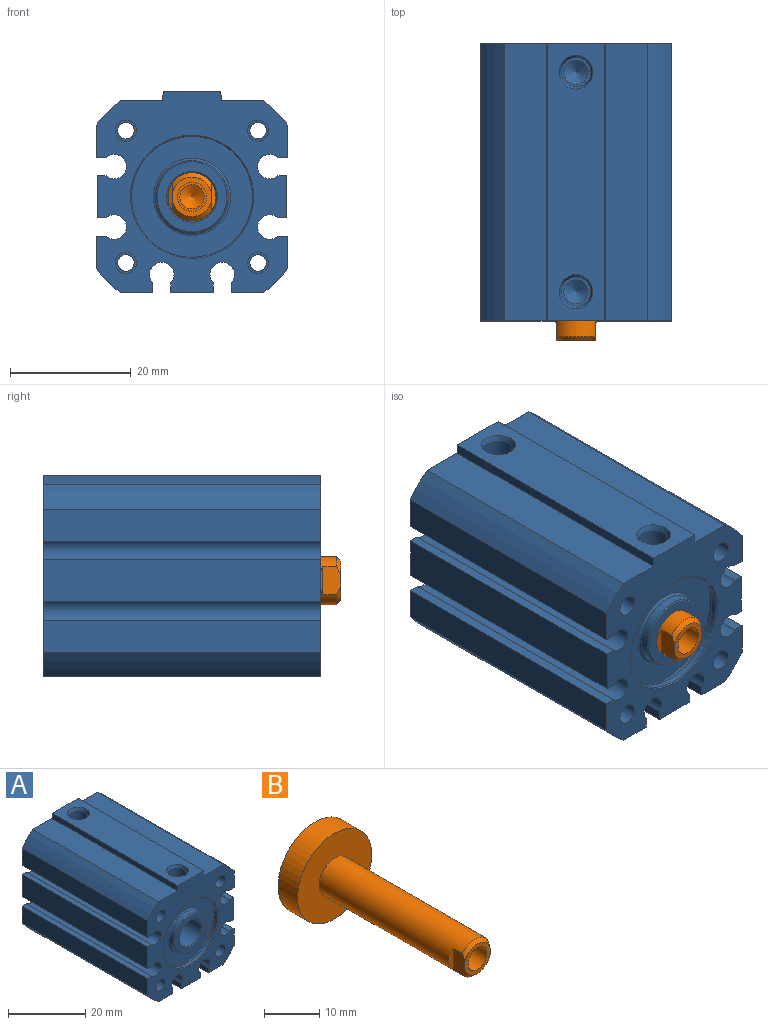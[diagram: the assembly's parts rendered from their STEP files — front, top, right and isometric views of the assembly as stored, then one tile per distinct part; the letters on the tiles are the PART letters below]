
ASSEMBLY  parts=2 mates=1
PART A: 85 faces, bbox 31.8x46x33.3 mm
  f0: cone r=10mm half-angle=45deg, axis (0,-1,0), area 17.9mm2, adj f34,f42
  f1: cone r=5.8mm half-angle=45deg, axis (0,1,0), area 10.5mm2, adj f32,f35
  f2: cone r=4.2mm half-angle=45deg, axis (0,-1,0), area 7.3mm2, adj f6,f35
  f3: cone r=9.03mm half-angle=30deg, axis (0,-1,0), area 28.7mm2, adj f4,f84
  f4: cone r=9.53mm half-angle=30deg, axis (0,1,0), area 29.5mm2, adj f3,f36
  f5: cylinder r=9.53mm len=30.4mm, axis (0,1,0), area 1819.4mm2, adj f82,f83
  f6: cylinder r=4mm len=8mm, axis (0,1,0), area 190.7mm2, adj f2,f82
  f7: cylinder r=1.75mm len=8.73mm, axis (0,1,0), area 96.1mm2, adj f36,f81
  f8: cylinder r=1.75mm len=8.73mm, axis (0,1,0), area 96.1mm2, adj f36,f80
  f9: cylinder r=1.75mm len=8.73mm, axis (0,1,0), area 96.1mm2, adj f36,f79
  f10: cylinder r=1.75mm len=8.73mm, axis (0,1,0), area 96.1mm2, adj f36,f78
  f11: cylinder r=1.75mm len=8.73mm, axis (0,-1,0), area 96.1mm2, adj f42,f77
  f12: cylinder r=1.75mm len=8.73mm, axis (0,-1,0), area 96.1mm2, adj f42,f76
  f13: cylinder r=1.75mm len=8.73mm, axis (0,-1,0), area 96.1mm2, adj f42,f75
  f14: cylinder r=1.75mm len=8.73mm, axis (0,-1,0), area 96.1mm2, adj f42,f74
  f15: cylinder r=1.38mm len=28.51mm, axis (0,-1,0), area 247.2mm2, adj f75,f79
  f16: cylinder r=1.38mm len=28.51mm, axis (0,-1,0), area 247.2mm2, adj f74,f78
  f17: cylinder r=1.38mm len=28.51mm, axis (0,-1,0), area 247.2mm2, adj f76,f80
  f18: cylinder r=1.38mm len=28.51mm, axis (0,-1,0), area 247.2mm2, adj f77,f81
  f19: cylinder r=2.02mm len=45.97mm, axis (0,-1,0), area 429.6mm2, adj f36,f42,f64,f65
  f20: cylinder r=2.02mm len=45.97mm, axis (0,-1,0), area 429.6mm2, adj f36,f42,f62,f63
  f21: cylinder r=2.02mm len=45.97mm, axis (0,-1,0), area 429.6mm2, adj f36,f42,f60,f61
  f22: cylinder r=2.02mm len=45.97mm, axis (0,-1,0), area 429.6mm2, adj f36,f42,f58,f59
  f23: cone r=2.02mm half-angle=59deg, axis (0,0,1), area 14.9mm2, adj f24
  f24: cylinder r=2.02mm len=4.04mm, axis (0,0,1), area 30.2mm2, adj f23,f57
  f25: cylinder r=2.41mm len=4.83mm, axis (0,0,1), area 46.5mm2, adj f26,f57
  f26: cone r=2.8mm half-angle=22.5deg, axis (0,0,1), area 16.6mm2, adj f25,f55
  f27: cone r=2.02mm half-angle=59deg, axis (0,0,1), area 14.9mm2, adj f28
  f28: cylinder r=2.02mm len=4.04mm, axis (0,0,1), area 30.2mm2, adj f27,f56
  f29: cylinder r=2.41mm len=4.83mm, axis (0,0,1), area 46.5mm2, adj f30,f56
  f30: cone r=2.8mm half-angle=22.5deg, axis (0,0,1), area 16.6mm2, adj f29,f55
  f31: torus R=6.4mm, axis (0,-1,0), area 24.3mm2, adj f32,f48
  f32: cylinder r=6mm len=12mm, axis (0,-1,0), area 57.5mm2, adj f1,f31
  f33: cylinder r=10.5mm len=21mm, axis (0,-1,0), area 64.3mm2, adj f47,f48
  f34: cylinder r=10mm len=20mm, axis (0,-1,0), area 59.7mm2, adj f0,f47
  f35: plane 11.6x11.6mm, normal (0,-1,0), area 50.3mm2, adj f1,f2
  f36: plane 33.34x31.75mm, normal (0,1,0), area 570.1mm2, adj f4,f7,f8,f9,f10,f19,f20,f21
  f37: plane 45.97x5.37mm, normal (1,0,0), area 246.7mm2, adj f36,f42,f52,f70
  f38: plane 45.97x5.37mm, normal (0,0,-1), area 246.7mm2, adj f36,f42,f49,f64
  f39: plane 45.97x7mm, normal (0,0,-1), area 321.8mm2, adj f36,f42,f62,f65
  f40: plane 45.97x5.37mm, normal (-1,0,0), area 246.7mm2, adj f36,f42,f50,f60
  f41: plane 45.97x6.98mm, normal (0,0,1), area 320.8mm2, adj f36,f42,f51,f54
  f42: plane 33.34x31.75mm, normal (0,-1,0), area 528.3mm2, adj f0,f11,f12,f13,f14,f19,f20,f21
  f43: plane 45.97x5.37mm, normal (-1,0,0), area 246.7mm2, adj f36,f42,f51,f59
  f44: plane 45.97x5.37mm, normal (0,0,-1), area 246.7mm2, adj f36,f42,f50,f63
  f45: plane 45.97x5.37mm, normal (1,0,0), area 246.7mm2, adj f36,f42,f49,f68
  f46: plane 45.97x6.98mm, normal (0,0,1), area 320.8mm2, adj f36,f42,f52,f53
  f47: plane 21x21mm, normal (0,1,0), area 32.2mm2, adj f33,f34
  f48: plane 21x21mm, normal (0,-1,0), area 217.7mm2, adj f31,f33
  f49: cylinder r=19.82mm len=45.97mm, axis (0,-1,0), area 261.5mm2, adj f36,f38,f42,f45
  f50: cylinder r=19.82mm len=45.97mm, axis (0,-1,0), area 261.5mm2, adj f36,f40,f42,f44
  f51: cylinder r=19.82mm len=45.97mm, axis (0,-1,0), area 261.5mm2, adj f36,f41,f42,f43
  f52: cylinder r=19.82mm len=45.97mm, axis (0,-1,0), area 261.5mm2, adj f36,f37,f42,f46
  f53: plane 45.97x1.59mm, normal (1,0,0.09), area 73.4mm2, adj f36,f42,f46,f55
  f54: plane 45.97x1.59mm, normal (-1,0,0.09), area 73.4mm2, adj f36,f41,f42,f55
  f55: plane 45.97x9.5mm, normal (0,0,1), area 387.5mm2, adj f26,f30,f36,f42,f53,f54
  f56: plane 4.83x4.83mm, normal (0,0,1), area 5.5mm2, adj f28,f29
  f57: plane 4.83x4.83mm, normal (0,0,1), area 5.5mm2, adj f24,f25
  f58: plane 45.97x1.49mm, normal (0,0,1), area 68.5mm2, adj f22,f36,f42,f73
  f59: plane 45.97x1.64mm, normal (0,0,-1), area 75.4mm2, adj f22,f36,f42,f43
  f60: plane 45.97x1.64mm, normal (0,0,1), area 75.4mm2, adj f21,f36,f40,f42
  f61: plane 45.97x1.49mm, normal (0,0,-1), area 68.5mm2, adj f21,f36,f42,f73
  f62: plane 45.97x1.64mm, normal (-1,0,0), area 75.4mm2, adj f20,f36,f39,f42
  f63: plane 45.97x1.64mm, normal (1,0,0), area 75.4mm2, adj f20,f36,f42,f44
  f64: plane 45.97x1.64mm, normal (-1,0,0), area 75.4mm2, adj f19,f36,f38,f42
  f65: plane 45.97x1.64mm, normal (1,0,0), area 75.4mm2, adj f19,f36,f39,f42
  f66: cylinder r=2.02mm len=45.97mm, axis (0,-1,0), area 429.6mm2, adj f36,f42,f67,f68
  f67: plane 45.97x1.49mm, normal (0,0,-1), area 68.5mm2, adj f36,f42,f66,f72
  f68: plane 45.97x1.64mm, normal (0,0,1), area 75.4mm2, adj f36,f42,f45,f66
  f69: cylinder r=2.02mm len=45.97mm, axis (0,-1,0), area 429.6mm2, adj f36,f42,f70,f71
  f70: plane 45.97x1.64mm, normal (0,0,-1), area 75.4mm2, adj f36,f37,f42,f69
  f71: plane 45.97x1.49mm, normal (0,0,1), area 68.5mm2, adj f36,f42,f69,f72
  f72: plane 45.97x7mm, normal (1,0,0), area 321.8mm2, adj f36,f42,f67,f71
  f73: plane 45.97x7mm, normal (-1,0,0), area 321.8mm2, adj f36,f42,f58,f61
  f74: plane 3.51x3.51mm, normal (0,-1,0), area 3.7mm2, adj f14,f16
  f75: plane 3.51x3.51mm, normal (0,-1,0), area 3.7mm2, adj f13,f15
  f76: plane 3.51x3.51mm, normal (0,-1,0), area 3.7mm2, adj f12,f17
  f77: plane 3.51x3.51mm, normal (0,-1,0), area 3.7mm2, adj f11,f18
  f78: plane 3.51x3.51mm, normal (0,1,0), area 3.7mm2, adj f10,f16
  f79: plane 3.51x3.51mm, normal (0,1,0), area 3.7mm2, adj f9,f15
  f80: plane 3.51x3.51mm, normal (0,1,0), area 3.7mm2, adj f8,f17
  f81: plane 3.51x3.51mm, normal (0,1,0), area 3.7mm2, adj f7,f18
  f82: plane 19.05x19.05mm, normal (0,1,0), area 234.8mm2, adj f5,f6
  f83: plane 19.05x19.05mm, normal (0,-1,0), area 285mm2, adj f5
  f84: plane 18.05x18.05mm, normal (0,1,0), area 255.9mm2, adj f3
PART B: 15 faces, bbox 19.2x41.8x19.2 mm
  f0: cylinder r=2.41mm len=11.68mm, axis (0,-1,0), area 177.1mm2, adj f8,f14
  f1: cylinder r=2.02mm len=4.04mm, axis (0,-1,0), area 4.4mm2, adj f2,f14
  f2: cone r=2.02mm half-angle=59deg, axis (0,-1,0), area 14.9mm2, adj f1
  f3: cylinder r=3.97mm len=35.79mm, axis (0,1,0), area 867.2mm2, adj f5,f6,f9,f10,f11,f12,f13
  f4: cylinder r=9.48mm len=18.95mm, axis (0,1,0), area 297.7mm2, adj f6,f7
  f5: cone r=3.27mm half-angle=45deg, axis (0,1,0), area 8.2mm2, adj f3,f8,f11,f13
  f6: plane 18.95x18.95mm, normal (0,-1,0), area 232.5mm2, adj f3,f4
  f7: plane 18.95x18.95mm, normal (0,1,0), area 282mm2, adj f4
  f8: plane 6.54x6.4mm, normal (0,-1,0), area 15.2mm2, adj f0,f5,f9,f11,f13
  f9: cone r=3.27mm half-angle=45deg, axis (0,1,0), area 8.2mm2, adj f3,f8,f11,f13
  f10: plane 4.91x0.99mm, normal (-0.5,-0.87,0), area 2.8mm2, adj f3,f11
  f11: plane 4.98x3.28mm, normal (-1,0,0), area 13.1mm2, adj f3,f5,f8,f9,f10
  f12: plane 4.91x0.99mm, normal (0.5,-0.87,0), area 2.8mm2, adj f3,f13
  f13: plane 4.98x3.28mm, normal (1,0,0), area 13.1mm2, adj f3,f5,f8,f9,f12
  f14: plane 4.83x4.83mm, normal (0,-1,0), area 5.5mm2, adj f0,f1
PLACE A t=(0,25.4,0)mm fixed
PLACE B t=(0,40.6,0)mm
MATE slider A.f0 <-> B.f0  axis (0,-1,0) through (0,4.54,0)mm
